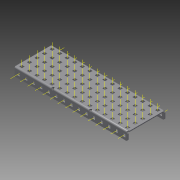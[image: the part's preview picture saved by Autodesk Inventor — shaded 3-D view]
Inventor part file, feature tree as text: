
AUTODESK INVENTOR PART (.ipt)
format: ipt  version: 2015 (Build 190159000, 159)  size: 2,528,256 bytes
history: native  units: in
note: dims shown in document units (in); Inventor stores cm internally (conversion verified against a paired STEP export)
features: other x111, pattern_linear x2, sheet_metal_op x1, extrude x1, imported_body x1, sketch x1
ambient origin geometry x8: Origin, YZ Plane, XZ Plane, XY Plane, X Axis, Y Axis, Z Axis, Center Point
bodies: Body1 (feature_tree)
feature tree (117):
  sheet_metal_op  "Fold1"
  other  "C-Channel"
  extrude  "length cut"  Depth=0.5in
  other  "top axis"
  other  "front axis"
  other  "back axis"
  pattern_linear  "top axes"  Spacing1=0.5in  [1 undecoded]
  pattern_linear  "horiz axes"  Spacing1=0.0in  [1 undecoded]
  other  "right plane"
  imported_body  "Base1"
  sketch  "Sketch1"  dims[d1=0.0in d4=0.5in d5=1.9685in d7=0.5in d10=0.5in d11=0.0in d12=0.0in d13=0.0in d14=-7.5in d15=0.0in d16=0.0in]
  other  "Work Point1"
  other  "Work Axis6"
  other  "Work Axis11"
  other  "Work Axis16"
  other  "Work Axis21"
  other  "Work Point2"
  other  "Work Point3"
  other  "Work Axis36"
  other  "Work Axis37"
  other  "Work Axis38"
  other  "Work Axis39"
  other  "Work Axis40"
  other  "Work Axis41"
  other  "Work Axis60"
  other  "Work Axis61"
  other  "Work Axis62"
  other  "Work Axis63"
  other  "Work Axis64"
  other  "Work Axis65"
  other  "Work Axis84"
  other  "Work Axis85"
  other  "Work Axis86"
  other  "Work Axis87"
  other  "Work Axis88"
  other  "Work Axis89"
  other  "Work Axis108"
  other  "Work Axis109"
  other  "Work Axis110"
  other  "Work Axis111"
  other  "Work Axis112"
  other  "Work Axis113"
  other  "Work Axis132"
  other  "Work Axis133"
  other  "Work Axis134"
  other  "Work Axis135"
  other  "Work Axis136"
  other  "Work Axis137"
  other  "Work Axis156"
  other  "Work Axis157"
  other  "Work Axis158"
  other  "Work Axis159"
  other  "Work Axis160"
  other  "Work Axis161"
  other  "Work Axis180"
  other  "Work Axis181"
  other  "Work Axis182"
  other  "Work Axis183"
  other  "Work Axis184"
  other  "Work Axis185"
  other  "Work Axis204"
  other  "Work Axis205"
  other  "Work Axis206"
  other  "Work Axis207"
  other  "Work Axis208"
  other  "Work Axis209"
  other  "Work Axis210"
  other  "Work Axis211"
  other  "Work Axis232"
  other  "Work Axis233"
  other  "Work Axis234"
  other  "Work Axis235"
  other  "Work Axis236"
  other  "Work Axis237"
  other  "Work Axis238"
  other  "Work Axis239"
  other  "Work Axis260"
  other  "Work Axis261"
  other  "Work Axis262"
  other  "Work Axis263"
  other  "Work Axis264"
  other  "Work Axis265"
  other  "Work Axis266"
  other  "Work Axis267"
  other  "Work Axis288"
  other  "Work Axis289"
  other  "Work Axis290"
  other  "Work Axis291"
  other  "Work Axis292"
  other  "Work Axis293"
  other  "Work Axis294"
  other  "Work Axis295"
  other  "Work Axis316"
  other  "Work Axis317"
  other  "Work Axis318"
  other  "Work Axis319"
  other  "Work Axis320"
  other  "Work Axis321"
  other  "Work Axis322"
  other  "Work Axis323"
  other  "Work Axis344"
  other  "Work Axis345"
  other  "Work Axis346"
  other  "Work Axis347"
  other  "Work Axis348"
  other  "Work Axis349"
  other  "Work Axis350"
  other  "Work Axis351"
  other  "Work Axis372"
  other  "Work Axis373"
  other  "Work Axis374"
  other  "Work Axis375"
  other  "Work Axis376"
  other  "Work Axis377"
  other  "Work Axis378"
  other  "Work Axis379"
  other  "left plane"
note: 2 required parameter values undecoded (feature->parameter linkage not recoverable at this tier; creation-order binding heuristic only, values carry confidence <= 0.55)
